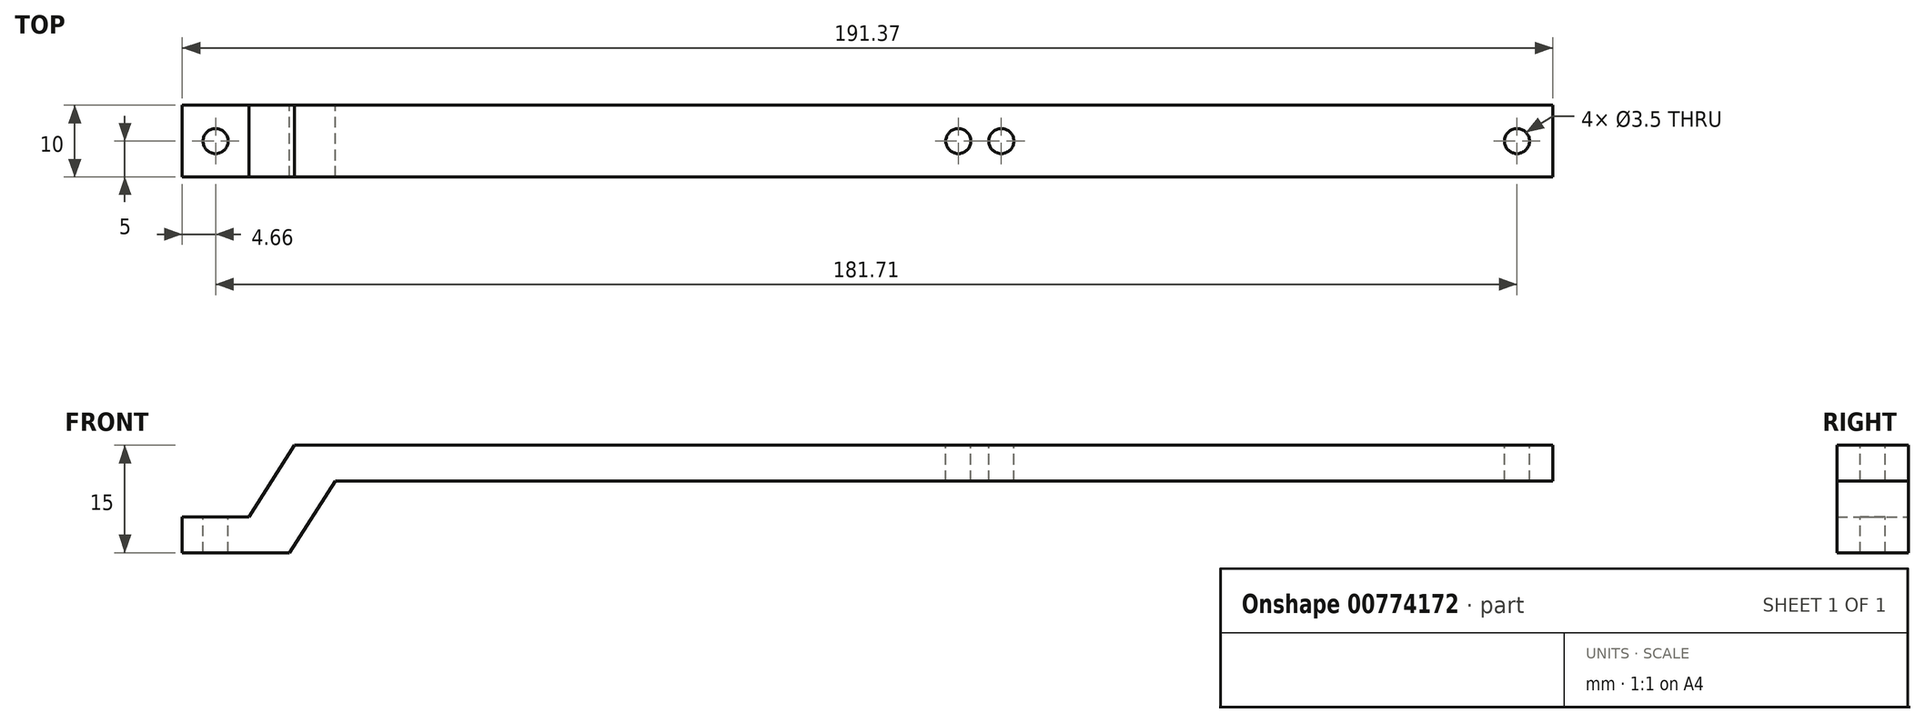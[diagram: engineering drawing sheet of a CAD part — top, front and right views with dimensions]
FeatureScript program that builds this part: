
annotation { "Feature Type Name" : "Feature", "Feature Type Description" : "" }
export const myFeature = defineFeature(function(context is Context, id is Id, definition is map)
    precondition{}
    {
        {
            var Q0;
            Q0=qCreatedBy(makeId("Front.planeOp"),FACE);
            var sketch = newSketch(context, id + "F0", { "sketchPlane" : qUnion([Q0])});
            skLineSegment(sketch, "E0", {"start": v(201.71, 10) * mm, "end": v(31.71, 10) * mm});
            skLineSegment(sketch, "E1", {"start": v(201.71, 10) * mm, "end": v(201.71, 15) * mm});
            skLineSegment(sketch, "E2", {"start": v(31.71, 10) * mm, "end": v(25.34, 0) * mm});
            skLineSegment(sketch, "E3", {"start": v(25.34, 0) * mm, "end": v(10.34, 0) * mm});
            skLineSegment(sketch, "E4", {"start": v(10.34, 0) * mm, "end": v(10.34, 5) * mm});
            skLineSegment(sketch, "E5", {"start": v(10.34, 5) * mm, "end": v(19.66, 5) * mm});
            skLineSegment(sketch, "E6", {"start": v(19.66, 5) * mm, "end": v(26.03, 15) * mm});
            skLineSegment(sketch, "E7", {"start": v(201.71, 15) * mm, "end": v(30.34, 15) * mm});
            skLineSegment(sketch, "E8", {"start": v(30.34, 15) * mm, "end": v(26.03, 15) * mm});
            skSolve(sketch);
        }
        {
            var Q0;
            Q0 = qSketchRegion(id + "F0", true);
            var Q1;
            Q1 = qSketchRegion(id + "F2", true);
            extrude(context, id + "F1", {"entities" : qUnion([Q0, Q1]), "depth" : 10 * mm, "offsetDistance" : 25 * mm});
        }
        {
            var Q0;
            Q0=makeQuery(id+"F1.opExtrude","SWEPT_FACE",FACE,{"disambiguationData":[OSD([sQuery(id+"F0.wireOp",EDGE,"E7"),sQuery(id+"F0.wireOp",EDGE,"E8")])]});
            var sketch = newSketch(context, id + "F2", { "sketchPlane" : qUnion([Q0])});
            skCircle(sketch, "E9", {"center": v(196.71, -5) * mm, "radius": 1.75 * mm});
            skCircle(sketch, "E10", {"center": v(118.71, -5) * mm, "radius": 1.75 * mm});
            skCircle(sketch, "E11", {"center": v(124.71, -5) * mm, "radius": 1.75 * mm});
            skLineSegment(sketch, "E12", {"start": v(201.71, -5) * mm, "end": v(118.71, -5) * mm, "construction": true});
            skLineSegment(sketch, "E13", {"start": v(201.71, -5) * mm, "end": v(196.71, -5) * mm, "construction": true});
            skLineSegment(sketch, "E14", {"start": v(201.71, -5) * mm, "end": v(124.71, -5) * mm, "construction": true});
            skSolve(sketch);
        }
        {
            var Q0;
            Q0=makeQuery(id+"F2.imprint","IMPRINT",FACE,{"disambiguationData":[TD([[makeQuery(id+"F2.imprint","IMPRINT",EDGE,{"derivedFrom":sQuery(id+"F2.wireOp",EDGE,"E10")}),1.0]])]});
            var Q1;
            Q1=makeQuery(id+"F2.imprint","IMPRINT",FACE,{"disambiguationData":[TD([[makeQuery(id+"F2.imprint","IMPRINT",EDGE,{"derivedFrom":sQuery(id+"F2.wireOp",EDGE,"E11")}),1.0]])]});
            var Q2;
            Q2=makeQuery(id+"F2.imprint","IMPRINT",FACE,{"disambiguationData":[TD([[makeQuery(id+"F2.imprint","IMPRINT",EDGE,{"derivedFrom":sQuery(id+"F2.wireOp",EDGE,"E9")}),1.0]])]});
            extrude(context, id + "F3", {"entities" : qUnion([Q0, Q1, Q2]), "operationType" : NewBodyOperationType.REMOVE, "endBound" : BoundingType.THROUGH_ALL, "oppositeDirection" : true, "depth" : 25 * mm, "offsetDistance" : 25 * mm});
        }
        {
            var Q0;
            Q0=makeQuery(id+"F1.opExtrude","SWEPT_FACE",FACE,{"disambiguationData":[OSD([sQuery(id+"F0.wireOp",EDGE,"E5")])]});
            var sketch = newSketch(context, id + "F4", { "sketchPlane" : qUnion([Q0])});
            skCircle(sketch, "E15", {"center": v(15, -5) * mm, "radius": 1.75 * mm});
            skLineSegment(sketch, "E16", {"start": v(15, -10) * mm, "end": v(15, 0) * mm, "construction": true});
            skLineSegment(sketch, "E17", {"start": v(10.34, -5) * mm, "end": v(15, -5) * mm});
            skSolve(sketch);
        }
        {
            var Q0;
            Q0=makeQuery(id+"F4.imprint","IMPRINT",FACE,{"disambiguationData":[TD([[makeQuery(id+"F4.imprint","IMPRINT",EDGE,{"derivedFrom":sQuery(id+"F4.wireOp",EDGE,"E15")}),1.0]])]});
            extrude(context, id + "F5", {"entities" : qUnion([Q0]), "operationType" : NewBodyOperationType.REMOVE, "endBound" : BoundingType.THROUGH_ALL, "oppositeDirection" : true, "depth" : 25 * mm, "offsetDistance" : 25 * mm});
        }
    });
